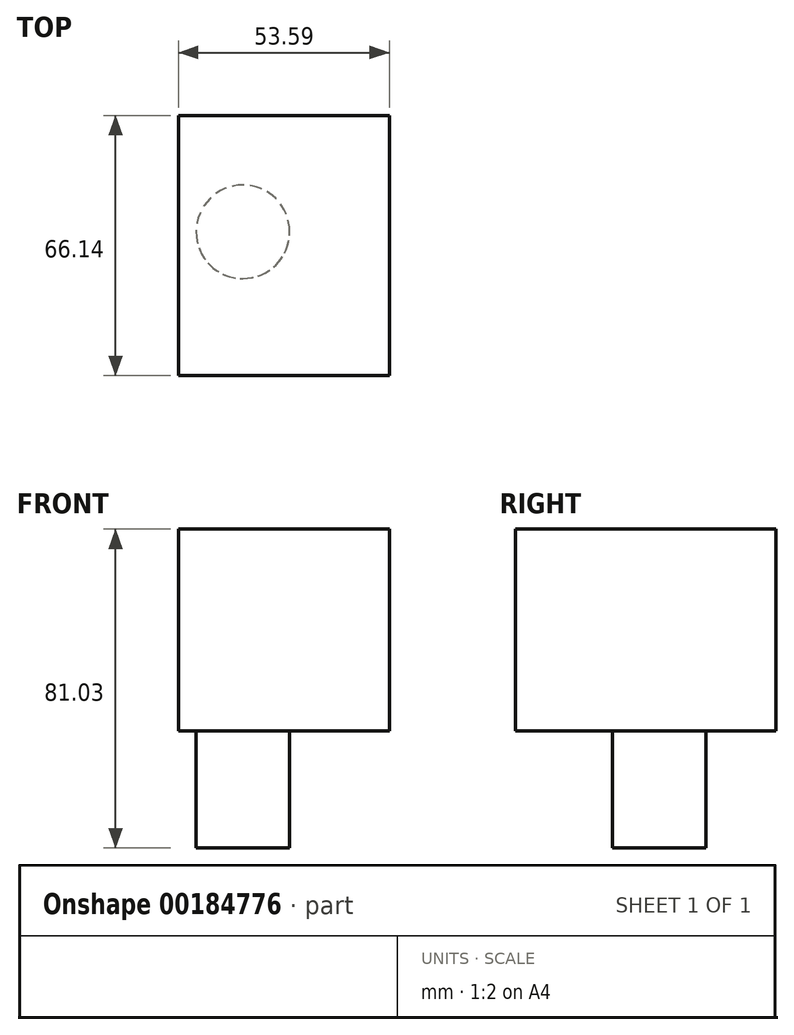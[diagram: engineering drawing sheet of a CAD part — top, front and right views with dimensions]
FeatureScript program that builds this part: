
annotation { "Feature Type Name" : "Feature", "Feature Type Description" : "" }
export const myFeature = defineFeature(function(context is Context, id is Id, definition is map)
    precondition{}
    {
        {
            var Q0;
            Q0=qCreatedBy(makeId("Right.planeOp"),FACE);
            var sketch = newSketch(context, id + "F0", { "sketchPlane" : qUnion([Q0])});
            skLineSegment(sketch, "E0.bottom", {"start": v(0, 6.07) * mm, "end": v(-66.14, 6.07) * mm});
            skLineSegment(sketch, "E0.top", {"start": v(0, 57.34) * mm, "end": v(-66.14, 57.34) * mm});
            skLineSegment(sketch, "E0.left", {"start": v(0, 6.07) * mm, "end": v(0, 57.34) * mm});
            skLineSegment(sketch, "E0.right", {"start": v(-66.14, 6.07) * mm, "end": v(-66.14, 57.34) * mm});
            skSolve(sketch);
        }
        {
            var Q0;
            Q0 = qSketchRegion(id + "F0", true);
            extrude(context, id + "F1", {"entities" : qUnion([Q0]), "depth" : 53.6 * mm});
        }
        {
            var Q0;
            Q0=makeQuery(id+"F1.opExtrude","SWEPT_FACE",FACE,{"disambiguationData":[OSD([sQuery(id+"F0.wireOp",EDGE,"E0.top")])]});
            var sketch = newSketch(context, id + "F2", { "sketchPlane" : qUnion([Q0])});
            skCircle(sketch, "E1", {"center": v(16.36, -29.57) * mm, "radius": 11.87 * mm});
            skSolve(sketch);
        }
        {
            var Q0;
            Q0 = qSketchRegion(id + "F2", true);
            extrude(context, id + "F3", {"entities" : qUnion([Q0]), "operationType" : NewBodyOperationType.ADD, "oppositeDirection" : true, "depth" : 81.03 * mm});
        }
    });
